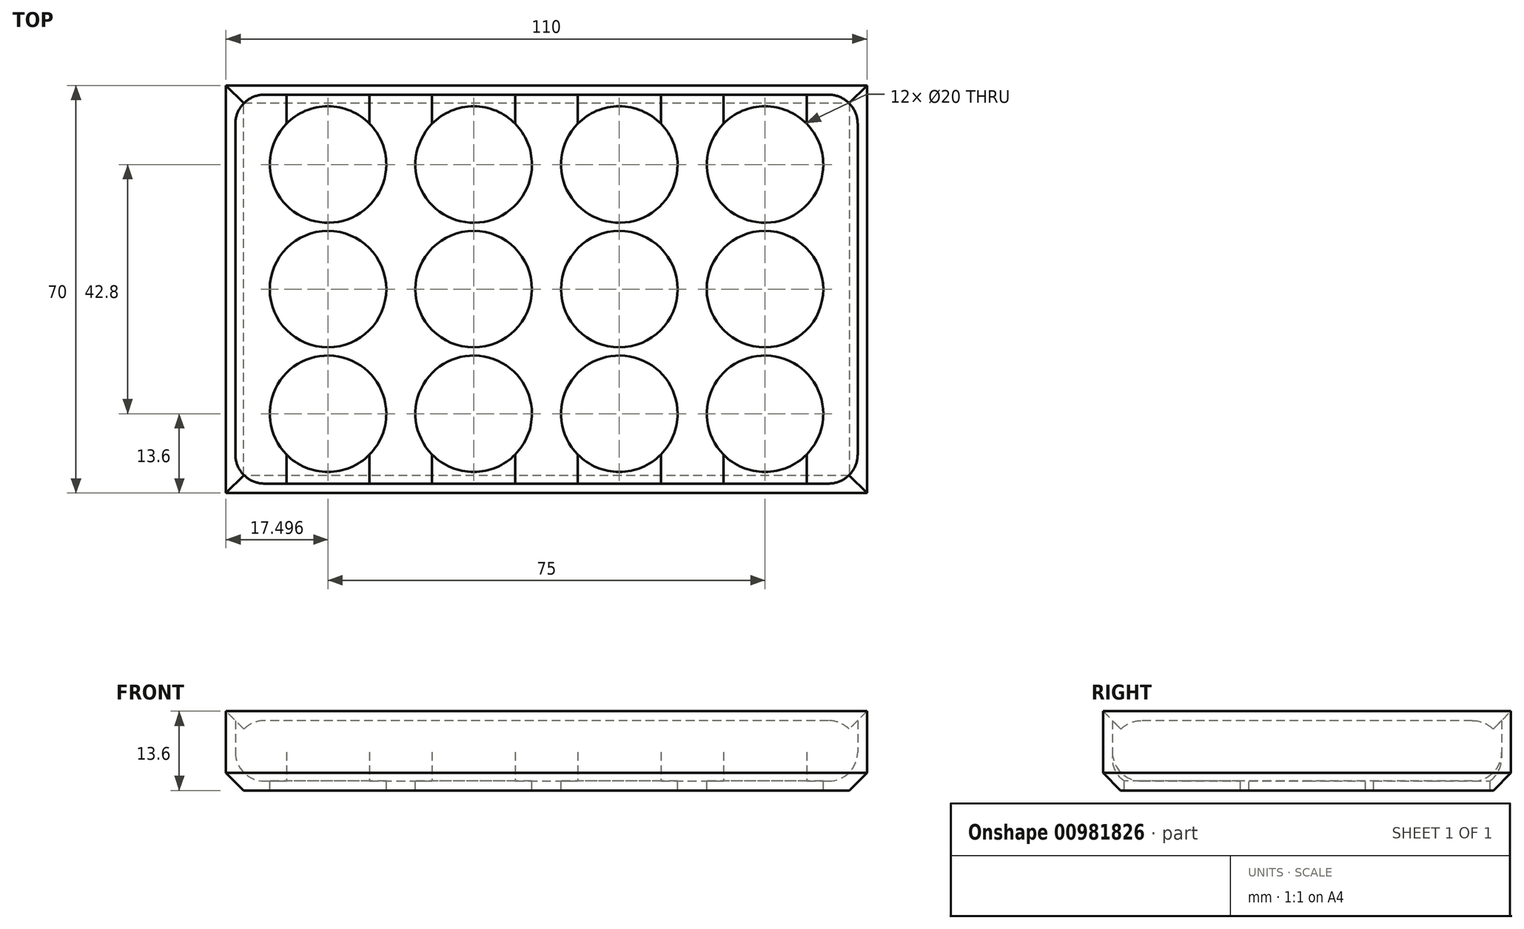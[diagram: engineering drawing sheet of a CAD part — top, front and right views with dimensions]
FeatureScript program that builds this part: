
annotation { "Feature Type Name" : "Feature", "Feature Type Description" : "" }
export const myFeature = defineFeature(function(context is Context, id is Id, definition is map)
    precondition{}
    {
        {
            var Q0;
            Q0=qCreatedBy(makeId("Top.planeOp"),FACE);
            var sketch = newSketch(context, id + "F0", { "sketchPlane" : qUnion([Q0])});
            skLineSegment(sketch, "E0.bottom", {"start": v(-42.8, 28.8) * mm, "end": v(67.2, 28.8) * mm});
            skLineSegment(sketch, "E0.top", {"start": v(-42.8, -41.2) * mm, "end": v(67.2, -41.2) * mm});
            skLineSegment(sketch, "E0.left", {"start": v(-42.8, 28.8) * mm, "end": v(-42.8, -41.2) * mm});
            skLineSegment(sketch, "E0.right", {"start": v(67.2, 28.8) * mm, "end": v(67.2, -41.2) * mm});
            skSolve(sketch);
        }
        {
            var Q0;
            Q0=makeQuery(id+"F0.imprint","IMPRINT",FACE,{"disambiguationData":[TD([[makeQuery(id+"F0.imprint","IMPRINT",EDGE,{"derivedFrom":sQuery(id+"F0.wireOp",EDGE,"E0.bottom")}),-1.0]])]});
            extrude(context, id + "F1", {"entities" : qUnion([Q0]), "depth" : 15 * mm, "offsetDistance" : 25 * mm});
        }
        {
            var Q0;
            Q0=makeQuery(id+"F1.opExtrude","CAP_FACE",FACE,{"disambiguationData":[OSD([sQuery(id+"F0.wireOp",EDGE,"E0.bottom"),sQuery(id+"F0.wireOp",EDGE,"E0.top"),sQuery(id+"F0.wireOp",EDGE,"E0.left"),sQuery(id+"F0.wireOp",EDGE,"E0.right")])],"isStart":false});
            shell(context, id + "F2", {"entities" : qUnion([Q0]), "thickness" : 1.6 * mm});
        }
        {
            var Q0;
            Q0=makeQuery(id+"F2.opShell","OFFSET_FACE",FACE,{"disambiguationData":[OSD([sQuery(id+"F0.wireOp",EDGE,"E0.bottom"),sQuery(id+"F0.wireOp",EDGE,"E0.top"),sQuery(id+"F0.wireOp",EDGE,"E0.left"),sQuery(id+"F0.wireOp",EDGE,"E0.right")])]});
            var sketch = newSketch(context, id + "F3", { "sketchPlane" : qUnion([Q0])});
            skCircle(sketch, "E1", {"center": v(49.7, 15.2) * mm, "radius": 10 * mm});
            skCircle(sketch, "E2.1.0.0", {"center": v(24.7, 15.2) * mm, "radius": 10 * mm});
            skCircle(sketch, "E2.2.0.0", {"center": v(-0.3, 15.2) * mm, "radius": 10 * mm});
            skCircle(sketch, "E2.3.0.0", {"center": v(-25.3, 15.2) * mm, "radius": 10 * mm});
            skLineSegment(sketch, "E2.direction1", {"start": v(49.7, 15.2) * mm, "end": v(24.7, 15.2) * mm, "construction": true});
            skCircle(sketch, "E3", {"center": v(49.7, -27.6) * mm, "radius": 10 * mm});
            skCircle(sketch, "E4.1.0.0", {"center": v(24.7, -27.6) * mm, "radius": 10 * mm});
            skCircle(sketch, "E4.2.0.0", {"center": v(-0.3, -27.6) * mm, "radius": 10 * mm});
            skCircle(sketch, "E4.3.0.0", {"center": v(-25.3, -27.6) * mm, "radius": 10 * mm});
            skLineSegment(sketch, "E4.direction1", {"start": v(49.7, -27.6) * mm, "end": v(24.7, -27.6) * mm, "construction": true});
            skCircle(sketch, "E5.2.0.0", {"center": v(-25.3, -6.2) * mm, "radius": 10 * mm});
            skCircle(sketch, "E6.1.0.0", {"center": v(-0.3, -6.2) * mm, "radius": 10 * mm});
            skCircle(sketch, "E6.2.0.0", {"center": v(24.7, -6.2) * mm, "radius": 10 * mm});
            skLineSegment(sketch, "E6.direction1", {"start": v(-25.3, -6.2) * mm, "end": v(-0.3, -6.2) * mm, "construction": true});
            skCircle(sketch, "E7.0.3.0", {"center": v(49.7, -6.2) * mm, "radius": 10 * mm});
            skSolve(sketch);
        }
        {
            var Q0;
            Q0=makeQuery(id+"F3.imprint","IMPRINT",FACE,{"disambiguationData":[TD([[makeQuery(id+"F3.imprint","IMPRINT",EDGE,{"derivedFrom":sQuery(id+"F3.wireOp",EDGE,"E2.3.0.0")}),1.0]])]});
            var Q1;
            Q1=makeQuery(id+"F3.imprint","IMPRINT",FACE,{"disambiguationData":[TD([[makeQuery(id+"F3.imprint","IMPRINT",EDGE,{"derivedFrom":sQuery(id+"F3.wireOp",EDGE,"E2.2.0.0")}),1.0]])]});
            var Q2;
            Q2=makeQuery(id+"F3.imprint","IMPRINT",FACE,{"disambiguationData":[TD([[makeQuery(id+"F3.imprint","IMPRINT",EDGE,{"derivedFrom":sQuery(id+"F3.wireOp",EDGE,"E2.1.0.0")}),1.0]])]});
            var Q3;
            Q3=makeQuery(id+"F3.imprint","IMPRINT",FACE,{"disambiguationData":[TD([[makeQuery(id+"F3.imprint","IMPRINT",EDGE,{"derivedFrom":sQuery(id+"F3.wireOp",EDGE,"E1")}),1.0]])]});
            var Q4;
            Q4=makeQuery(id+"F3.imprint","IMPRINT",FACE,{"disambiguationData":[TD([[makeQuery(id+"F3.imprint","IMPRINT",EDGE,{"derivedFrom":sQuery(id+"F3.wireOp",EDGE,"E6.2.0.0")}),1.0]])]});
            var Q5;
            Q5=makeQuery(id+"F3.imprint","IMPRINT",FACE,{"disambiguationData":[TD([[makeQuery(id+"F3.imprint","IMPRINT",EDGE,{"derivedFrom":sQuery(id+"F3.wireOp",EDGE,"E3")}),1.0]])]});
            var Q6;
            Q6=makeQuery(id+"F3.imprint","IMPRINT",FACE,{"disambiguationData":[TD([[makeQuery(id+"F3.imprint","IMPRINT",EDGE,{"derivedFrom":sQuery(id+"F3.wireOp",EDGE,"E4.1.0.0")}),1.0]])]});
            var Q7;
            Q7=makeQuery(id+"F3.imprint","IMPRINT",FACE,{"disambiguationData":[TD([[makeQuery(id+"F3.imprint","IMPRINT",EDGE,{"derivedFrom":sQuery(id+"F3.wireOp",EDGE,"E6.1.0.0")}),1.0]])]});
            var Q8;
            Q8=makeQuery(id+"F3.imprint","IMPRINT",FACE,{"disambiguationData":[TD([[makeQuery(id+"F3.imprint","IMPRINT",EDGE,{"derivedFrom":sQuery(id+"F3.wireOp",EDGE,"E4.2.0.0")}),1.0]])]});
            var Q9;
            Q9=makeQuery(id+"F3.imprint","IMPRINT",FACE,{"disambiguationData":[TD([[makeQuery(id+"F3.imprint","IMPRINT",EDGE,{"derivedFrom":sQuery(id+"F3.wireOp",EDGE,"E5.2.0.0")}),1.0]])]});
            var Q10;
            Q10=makeQuery(id+"F3.imprint","IMPRINT",FACE,{"disambiguationData":[TD([[makeQuery(id+"F3.imprint","IMPRINT",EDGE,{"derivedFrom":sQuery(id+"F3.wireOp",EDGE,"E4.3.0.0")}),1.0]])]});
            var Q11;
            Q11=makeQuery(id+"F3.imprint","IMPRINT",FACE,{"disambiguationData":[TD([[makeQuery(id+"F3.imprint","IMPRINT",EDGE,{"derivedFrom":sQuery(id+"F3.wireOp",EDGE,"E7.0.3.0")}),1.0]])]});
            extrude(context, id + "F4", {"entities" : qUnion([Q0, Q1, Q2, Q3, Q4, Q5, Q6, Q7, Q8, Q9, Q10, Q11]), "operationType" : NewBodyOperationType.REMOVE, "oppositeDirection" : true, "depth" : 5 * mm, "offsetDistance" : 25 * mm});
        }
        {
            var Q0;
            Q0=makeQuery(id+"F1.opExtrude","CAP_EDGE",EDGE,{"disambiguationData":[OSD([sQuery(id+"F0.wireOp",EDGE,"E0.left")])],"isStart":true});
            var Q1;
            Q1=makeQuery(id+"F1.opExtrude","CAP_EDGE",EDGE,{"disambiguationData":[OSD([sQuery(id+"F0.wireOp",EDGE,"E0.top")])],"isStart":true});
            var Q2;
            Q2=makeQuery(id+"F1.opExtrude","CAP_EDGE",EDGE,{"disambiguationData":[OSD([sQuery(id+"F0.wireOp",EDGE,"E0.right")])],"isStart":true});
            var Q3;
            Q3=makeQuery(id+"F1.opExtrude","CAP_EDGE",EDGE,{"disambiguationData":[OSD([sQuery(id+"F0.wireOp",EDGE,"E0.bottom")])],"isStart":true});
            chamfer(context, id + "F5", {"entities" : qUnion([Q0, Q1, Q2, Q3]), "width" : 3 * mm, "tangentPropagation" : true});
        }
        {
            var Q0;
            {var subQ0=sQuery(id+"F0.wireOp",EDGE,"E0.bottom");Q0=makeQuery(id+"F2.opShell","OFFSET_EDGE",EDGE,{"disambiguationData":[OSD([subQ0]),TDD([makeQuery(id+"F1.opExtrude","CAP_EDGE",EDGE,{"disambiguationData":[OSD([subQ0])],"isStart":false})])]});}
            var Q1;
            {var subQ0=sQuery(id+"F0.wireOp",EDGE,"E0.left");Q1=makeQuery(id+"F2.opShell","OFFSET_EDGE",EDGE,{"disambiguationData":[OSD([subQ0]),TDD([makeQuery(id+"F1.opExtrude","CAP_EDGE",EDGE,{"disambiguationData":[OSD([subQ0])],"isStart":false})])]});}
            var Q2;
            {var subQ0=sQuery(id+"F0.wireOp",EDGE,"E0.right");Q2=makeQuery(id+"F2.opShell","OFFSET_EDGE",EDGE,{"disambiguationData":[OSD([subQ0]),TDD([makeQuery(id+"F1.opExtrude","CAP_EDGE",EDGE,{"disambiguationData":[OSD([subQ0])],"isStart":false})])]});}
            var Q3;
            {var subQ0=sQuery(id+"F0.wireOp",EDGE,"E0.top");Q3=makeQuery(id+"F2.opShell","OFFSET_EDGE",EDGE,{"disambiguationData":[OSD([subQ0]),TDD([makeQuery(id+"F1.opExtrude","CAP_EDGE",EDGE,{"disambiguationData":[OSD([subQ0])],"isStart":false})])]});}
            chamfer(context, id + "F6", {"entities" : qUnion([Q0, Q1, Q2, Q3]), "width" : 3 * mm, "tangentPropagation" : true});
        }
        {
            var Q0;
            {var subQ0=sQuery(id+"F0.wireOp",EDGE,"E0.left");Q0=makeQuery(id+"F2.opShell","OFFSET_EDGE",EDGE,{"disambiguationData":[OSD([subQ0]),TDD([makeQuery(id+"F1.opExtrude","CAP_EDGE",EDGE,{"disambiguationData":[OSD([subQ0])],"isStart":true})])]});}
            var Q1;
            {var subQ0=sQuery(id+"F0.wireOp",EDGE,"E0.right");Q1=makeQuery(id+"F2.opShell","OFFSET_EDGE",EDGE,{"disambiguationData":[OSD([subQ0]),TDD([makeQuery(id+"F1.opExtrude","CAP_EDGE",EDGE,{"disambiguationData":[OSD([subQ0])],"isStart":true})])]});}
            fillet(context, id + "F7", {"entities" : qUnion([Q0, Q1]), "radius" : 5 * mm, "tangentPropagation" : true, "allowEdgeOverflow" : false});
        }
        {
            var Q0;
            {var subQ0=sQuery(id+"F3.wireOp",EDGE,"E1");var subQ1=sQuery(id+"F0.wireOp",EDGE,"E0.bottom");var subQ2=makeQuery(id+"F2.opShell","OFFSET_FACE",FACE,{"disambiguationData":[OSD([subQ1,sQuery(id+"F0.wireOp",EDGE,"E0.top"),sQuery(id+"F0.wireOp",EDGE,"E0.left"),sQuery(id+"F0.wireOp",EDGE,"E0.right")])]});var subQ3=makeQuery(id+"F2.opShell","OFFSET_FACE",FACE,{"disambiguationData":[OSD([subQ1])]});var subQ4=sQuery(id+"F3.wireOp",EDGE,"E2.1.0.0");Q0=makeQuery(id+"F4.boolean.opBoolean","SPLIT",EDGE,{"disambiguationData":[topologyDisambiguationEdgeConnected([subQ3,subQ2]),TD([subQ3,subQ2,makeQuery(id+"F4.opExtrude","SWEPT_FACE",FACE,{"disambiguationData":[OSD([subQ0])]}),makeQuery(id+"F4.opExtrude","CAP_FACE",FACE,{"disambiguationData":[OSD([subQ0])],"isStart":true}),makeQuery(id+"F4.opExtrude","SWEPT_FACE",FACE,{"disambiguationData":[OSD([subQ4])]}),makeQuery(id+"F4.opExtrude","CAP_FACE",FACE,{"disambiguationData":[OSD([subQ4])],"isStart":true})])],"derivedFrom":makeQuery(id+"F2.opShell","OFFSET_EDGE",EDGE,{"disambiguationData":[OSD([subQ1]),TDD([makeQuery(id+"F1.opExtrude","CAP_EDGE",EDGE,{"disambiguationData":[OSD([subQ1])],"isStart":true})])]})});}
            var Q1;
            {var subQ0=sQuery(id+"F3.wireOp",EDGE,"E2.1.0.0");var subQ1=sQuery(id+"F0.wireOp",EDGE,"E0.bottom");var subQ2=makeQuery(id+"F2.opShell","OFFSET_FACE",FACE,{"disambiguationData":[OSD([subQ1,sQuery(id+"F0.wireOp",EDGE,"E0.top"),sQuery(id+"F0.wireOp",EDGE,"E0.left"),sQuery(id+"F0.wireOp",EDGE,"E0.right")])]});var subQ3=sQuery(id+"F3.wireOp",EDGE,"E2.2.0.0");var subQ4=makeQuery(id+"F2.opShell","OFFSET_FACE",FACE,{"disambiguationData":[OSD([subQ1])]});Q1=makeQuery(id+"F4.boolean.opBoolean","SPLIT",EDGE,{"disambiguationData":[topologyDisambiguationEdgeConnected([subQ4,subQ2]),TD([subQ4,subQ2,makeQuery(id+"F4.opExtrude","SWEPT_FACE",FACE,{"disambiguationData":[OSD([subQ0])]}),makeQuery(id+"F4.opExtrude","CAP_FACE",FACE,{"disambiguationData":[OSD([subQ0])],"isStart":true}),makeQuery(id+"F4.opExtrude","SWEPT_FACE",FACE,{"disambiguationData":[OSD([subQ3])]}),makeQuery(id+"F4.opExtrude","CAP_FACE",FACE,{"disambiguationData":[OSD([subQ3])],"isStart":true})])],"derivedFrom":makeQuery(id+"F2.opShell","OFFSET_EDGE",EDGE,{"disambiguationData":[OSD([subQ1]),TDD([makeQuery(id+"F1.opExtrude","CAP_EDGE",EDGE,{"disambiguationData":[OSD([subQ1])],"isStart":true})])]})});}
            var Q2;
            {var subQ0=sQuery(id+"F3.wireOp",EDGE,"E2.2.0.0");var subQ1=sQuery(id+"F0.wireOp",EDGE,"E0.bottom");var subQ2=makeQuery(id+"F2.opShell","OFFSET_FACE",FACE,{"disambiguationData":[OSD([subQ1,sQuery(id+"F0.wireOp",EDGE,"E0.top"),sQuery(id+"F0.wireOp",EDGE,"E0.left"),sQuery(id+"F0.wireOp",EDGE,"E0.right")])]});var subQ3=makeQuery(id+"F2.opShell","OFFSET_FACE",FACE,{"disambiguationData":[OSD([subQ1])]});var subQ4=sQuery(id+"F3.wireOp",EDGE,"E2.3.0.0");Q2=makeQuery(id+"F4.boolean.opBoolean","SPLIT",EDGE,{"disambiguationData":[topologyDisambiguationEdgeConnected([subQ3,subQ2]),TD([subQ3,subQ2,makeQuery(id+"F4.opExtrude","SWEPT_FACE",FACE,{"disambiguationData":[OSD([subQ0])]}),makeQuery(id+"F4.opExtrude","CAP_FACE",FACE,{"disambiguationData":[OSD([subQ0])],"isStart":true}),makeQuery(id+"F4.opExtrude","SWEPT_FACE",FACE,{"disambiguationData":[OSD([subQ4])]}),makeQuery(id+"F4.opExtrude","CAP_FACE",FACE,{"disambiguationData":[OSD([subQ4])],"isStart":true})])],"derivedFrom":makeQuery(id+"F2.opShell","OFFSET_EDGE",EDGE,{"disambiguationData":[OSD([subQ1]),TDD([makeQuery(id+"F1.opExtrude","CAP_EDGE",EDGE,{"disambiguationData":[OSD([subQ1])],"isStart":true})])]})});}
            var Q3;
            {var subQ0=sQuery(id+"F3.wireOp",EDGE,"E3");var subQ1=sQuery(id+"F0.wireOp",EDGE,"E0.top");var subQ2=makeQuery(id+"F2.opShell","OFFSET_FACE",FACE,{"disambiguationData":[OSD([subQ1])]});var subQ3=makeQuery(id+"F2.opShell","OFFSET_FACE",FACE,{"disambiguationData":[OSD([sQuery(id+"F0.wireOp",EDGE,"E0.bottom"),subQ1,sQuery(id+"F0.wireOp",EDGE,"E0.left"),sQuery(id+"F0.wireOp",EDGE,"E0.right")])]});var subQ4=sQuery(id+"F3.wireOp",EDGE,"E4.1.0.0");Q3=makeQuery(id+"F4.boolean.opBoolean","SPLIT",EDGE,{"disambiguationData":[topologyDisambiguationEdgeConnected([subQ3,subQ2]),TD([subQ3,subQ2,makeQuery(id+"F4.opExtrude","SWEPT_FACE",FACE,{"disambiguationData":[OSD([subQ0])]}),makeQuery(id+"F4.opExtrude","CAP_FACE",FACE,{"disambiguationData":[OSD([subQ0])],"isStart":true}),makeQuery(id+"F4.opExtrude","SWEPT_FACE",FACE,{"disambiguationData":[OSD([subQ4])]}),makeQuery(id+"F4.opExtrude","CAP_FACE",FACE,{"disambiguationData":[OSD([subQ4])],"isStart":true})])],"derivedFrom":makeQuery(id+"F2.opShell","OFFSET_EDGE",EDGE,{"disambiguationData":[OSD([subQ1]),TDD([makeQuery(id+"F1.opExtrude","CAP_EDGE",EDGE,{"disambiguationData":[OSD([subQ1])],"isStart":true})])]})});}
            var Q4;
            {var subQ0=sQuery(id+"F3.wireOp",EDGE,"E4.1.0.0");var subQ1=sQuery(id+"F0.wireOp",EDGE,"E0.top");var subQ2=makeQuery(id+"F2.opShell","OFFSET_FACE",FACE,{"disambiguationData":[OSD([subQ1])]});var subQ3=sQuery(id+"F3.wireOp",EDGE,"E4.2.0.0");var subQ4=makeQuery(id+"F2.opShell","OFFSET_FACE",FACE,{"disambiguationData":[OSD([sQuery(id+"F0.wireOp",EDGE,"E0.bottom"),subQ1,sQuery(id+"F0.wireOp",EDGE,"E0.left"),sQuery(id+"F0.wireOp",EDGE,"E0.right")])]});Q4=makeQuery(id+"F4.boolean.opBoolean","SPLIT",EDGE,{"disambiguationData":[topologyDisambiguationEdgeConnected([subQ4,subQ2]),TD([subQ4,subQ2,makeQuery(id+"F4.opExtrude","SWEPT_FACE",FACE,{"disambiguationData":[OSD([subQ0])]}),makeQuery(id+"F4.opExtrude","CAP_FACE",FACE,{"disambiguationData":[OSD([subQ0])],"isStart":true}),makeQuery(id+"F4.opExtrude","SWEPT_FACE",FACE,{"disambiguationData":[OSD([subQ3])]}),makeQuery(id+"F4.opExtrude","CAP_FACE",FACE,{"disambiguationData":[OSD([subQ3])],"isStart":true})])],"derivedFrom":makeQuery(id+"F2.opShell","OFFSET_EDGE",EDGE,{"disambiguationData":[OSD([subQ1]),TDD([makeQuery(id+"F1.opExtrude","CAP_EDGE",EDGE,{"disambiguationData":[OSD([subQ1])],"isStart":true})])]})});}
            var Q5;
            {var subQ0=sQuery(id+"F3.wireOp",EDGE,"E4.2.0.0");var subQ1=sQuery(id+"F0.wireOp",EDGE,"E0.top");var subQ2=makeQuery(id+"F2.opShell","OFFSET_FACE",FACE,{"disambiguationData":[OSD([subQ1])]});var subQ3=makeQuery(id+"F2.opShell","OFFSET_FACE",FACE,{"disambiguationData":[OSD([sQuery(id+"F0.wireOp",EDGE,"E0.bottom"),subQ1,sQuery(id+"F0.wireOp",EDGE,"E0.left"),sQuery(id+"F0.wireOp",EDGE,"E0.right")])]});var subQ4=sQuery(id+"F3.wireOp",EDGE,"E4.3.0.0");Q5=makeQuery(id+"F4.boolean.opBoolean","SPLIT",EDGE,{"disambiguationData":[topologyDisambiguationEdgeConnected([subQ3,subQ2]),TD([subQ3,subQ2,makeQuery(id+"F4.opExtrude","SWEPT_FACE",FACE,{"disambiguationData":[OSD([subQ0])]}),makeQuery(id+"F4.opExtrude","CAP_FACE",FACE,{"disambiguationData":[OSD([subQ0])],"isStart":true}),makeQuery(id+"F4.opExtrude","SWEPT_FACE",FACE,{"disambiguationData":[OSD([subQ4])]}),makeQuery(id+"F4.opExtrude","CAP_FACE",FACE,{"disambiguationData":[OSD([subQ4])],"isStart":true})])],"derivedFrom":makeQuery(id+"F2.opShell","OFFSET_EDGE",EDGE,{"disambiguationData":[OSD([subQ1]),TDD([makeQuery(id+"F1.opExtrude","CAP_EDGE",EDGE,{"disambiguationData":[OSD([subQ1])],"isStart":true})])]})});}
            fillet(context, id + "F8", {"entities" : qUnion([Q0, Q1, Q2, Q3, Q4, Q5]), "radius" : 5 * mm, "tangentPropagation" : true, "allowEdgeOverflow" : false});
        }
    });
